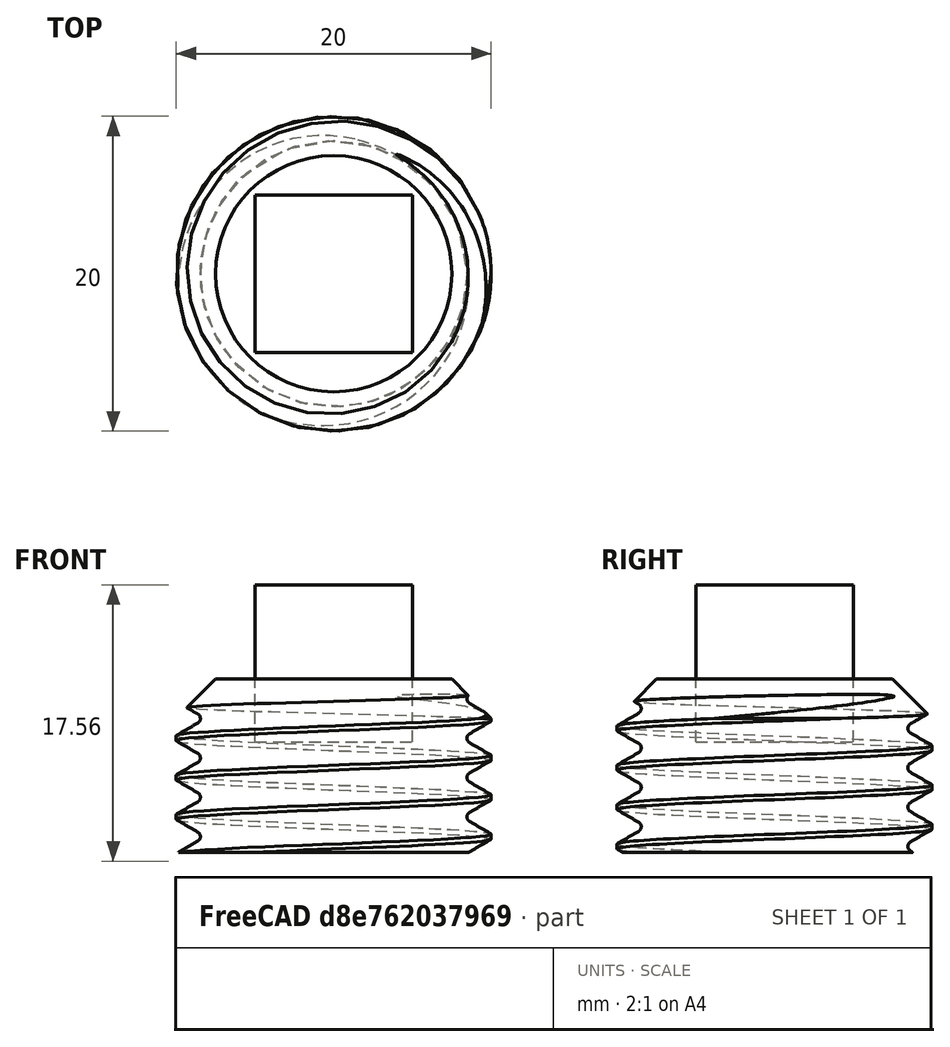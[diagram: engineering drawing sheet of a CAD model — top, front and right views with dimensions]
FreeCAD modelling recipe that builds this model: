
FCSTD DOCUMENT  (FreeCAD 1.0R39285 (Git))
Label: Оснастка для гайки
License: All rights reserved
LicenseURL: https://en.wikipedia.org/wiki/All_rights_reserved
objects: Part::Box×2, Part::FeaturePython×1, Part::Cut×1
note: 4 computed .brp shape members not serialized (recipe doc carries the construction recipe); baked Part::Feature solids carry a one-line shape summary decoded from their .brp

FEATURE [Part::FeaturePython] ThreadedRod  label="M20x20-Шпилька"  # WARN: FeaturePython — macro-defined, semantics opaque (R4)
  Diameter = 15
  DiameterCustom = 6
  Invert = false
  LeftHanded = false
  Length = 20
  MatchOuter = false
  OffsetAngle = 0
  PitchCustom = 1
  Thread = true
  Type = 4
FEATURE [Part::Box] Box  label="Куб"
  AttacherType = Attacher::AttachEngine3D
  Height = 10
  Length = 10
  Placement = pos=(-5,-5,-4) rot=(0,0,1;0rad)
  Width = 10
FEATURE [Part::Box] Box001  label="Куб001"
  AttacherType = Attacher::AttachEngine3D
  Height = 20
  Length = 48
  Placement = pos=(-25,-16,-31) rot=(0,0,1;0rad)
  Width = 50
FEATURE [Part::Cut] Cut
  Base = -> ThreadedRod
  Tool = -> Box001
